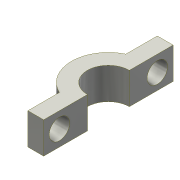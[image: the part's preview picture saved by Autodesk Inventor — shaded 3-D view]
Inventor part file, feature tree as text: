
AUTODESK INVENTOR PART (.ipt)
format: ipt  version: 2021 (Build 250183000, 183)  size: 113,152 bytes
history: native  units: mm
features: sketch x2, other x1, extrude x1, hole x1, mirror x1, projected_geometry x1
ambient origin geometry x8: Origin, YZ Plane, XZ Plane, XY Plane, X Axis, Y Axis, Z Axis, Center Point
bodies: Body1 (feature_tree)
feature tree (7):
  other  "Твердое тело1"
  extrude  "Выдавливание1"  Depth=4.0mm
  hole  "Отверстие1"  [1 undecoded]
  mirror  "Зеркальное отражение1"
  sketch  "Эскиз1"
  sketch  "Эскиз2"
  projected_geometry  "Спроецированная петля1"
note: 1 required parameter value undecoded (feature->parameter linkage not recoverable at this tier; creation-order binding heuristic only, values carry confidence <= 0.55)
